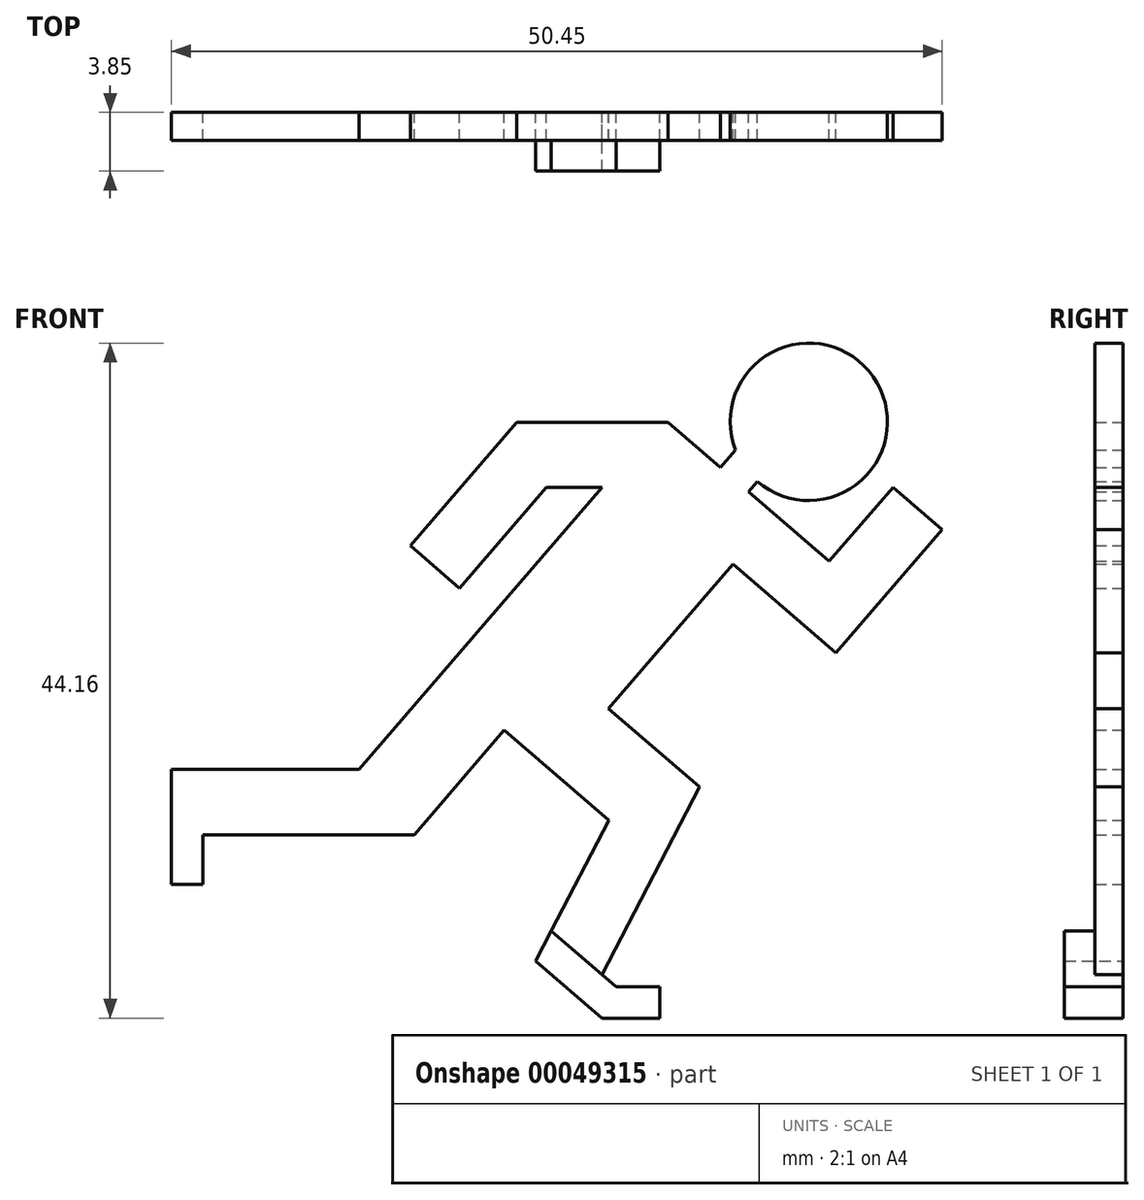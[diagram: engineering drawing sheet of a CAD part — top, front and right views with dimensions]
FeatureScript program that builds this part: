
annotation { "Feature Type Name" : "Feature", "Feature Type Description" : "" }
export const myFeature = defineFeature(function(context is Context, id is Id, definition is map)
    precondition{}
    {
        {
            var Q0;
            Q0=qCreatedBy(makeId("Front.planeOp"),FACE);
            var sketch = newSketch(context, id + "F0", { "sketchPlane" : qUnion([Q0])});
            skCircle(sketch, "E0", {"center": v(13.54, 39.01) * mm, "radius": 5.15 * mm});
            skLineSegment(sketch, "E1", {"start": v(0, 0) * mm, "end": v(3.79, 0) * mm});
            skLineSegment(sketch, "E2", {"start": v(3.79, 0) * mm, "end": v(3.79, 2.06) * mm});
            skLineSegment(sketch, "E3", {"start": v(3.79, 2.06) * mm, "end": v(0.92, 2.06) * mm});
            skLineSegment(sketch, "E4", {"start": v(0.92, 2.06) * mm, "end": v(0, 2.85) * mm});
            skLineSegment(sketch, "E5", {"start": v(0, 2.85) * mm, "end": v(6.38, 15.12) * mm});
            skLineSegment(sketch, "E6", {"start": v(6.38, 15.12) * mm, "end": v(0.43, 20.24) * mm});
            skLineSegment(sketch, "E7", {"start": v(0.43, 20.24) * mm, "end": v(8.57, 29.7) * mm});
            skLineSegment(sketch, "E8", {"start": v(8.57, 29.7) * mm, "end": v(15.32, 23.88) * mm});
            skLineSegment(sketch, "E9", {"start": v(15.32, 23.88) * mm, "end": v(22.27, 31.95) * mm});
            skLineSegment(sketch, "E10", {"start": v(22.27, 31.95) * mm, "end": v(19.04, 34.73) * mm});
            skLineSegment(sketch, "E11", {"start": v(19.04, 34.73) * mm, "end": v(14.87, 29.89) * mm});
            skLineSegment(sketch, "E12", {"start": v(14.87, 29.89) * mm, "end": v(4.32, 38.97) * mm});
            skLineSegment(sketch, "E13", {"start": v(4.32, 38.97) * mm, "end": v(-5.59, 38.97) * mm});
            skLineSegment(sketch, "E14", {"start": v(-5.59, 38.97) * mm, "end": v(-12.54, 30.9) * mm});
            skLineSegment(sketch, "E15", {"start": v(-12.54, 30.9) * mm, "end": v(-9.31, 28.12) * mm});
            skLineSegment(sketch, "E16", {"start": v(-9.31, 28.12) * mm, "end": v(-3.64, 34.71) * mm});
            skLineSegment(sketch, "E17", {"start": v(-3.64, 34.71) * mm, "end": v(0, 34.71) * mm});
            skLineSegment(sketch, "E18", {"start": v(0, 34.71) * mm, "end": v(-15.9, 16.26) * mm});
            skLineSegment(sketch, "E19", {"start": v(-15.9, 16.26) * mm, "end": v(-28.18, 16.26) * mm});
            skLineSegment(sketch, "E20", {"start": v(-28.18, 16.26) * mm, "end": v(-28.18, 8.74) * mm});
            skLineSegment(sketch, "E21", {"start": v(-28.18, 8.74) * mm, "end": v(-26.12, 8.74) * mm});
            skLineSegment(sketch, "E22", {"start": v(-26.12, 8.74) * mm, "end": v(-26.12, 12) * mm});
            skLineSegment(sketch, "E23", {"start": v(-26.12, 12) * mm, "end": v(-12.29, 12) * mm});
            skLineSegment(sketch, "E24", {"start": v(-12.29, 12) * mm, "end": v(-6.4, 18.85) * mm});
            skLineSegment(sketch, "E25", {"start": v(-6.4, 18.85) * mm, "end": v(0.45, 12.95) * mm});
            skLineSegment(sketch, "E26", {"start": v(0.45, 12.95) * mm, "end": v(-4.34, 3.74) * mm});
            skLineSegment(sketch, "E27", {"start": v(-4.34, 3.74) * mm, "end": v(0, 0) * mm});
            skLineSegment(sketch, "E28", {"start": v(0, 34.71) * mm, "end": v(0, 38.97) * mm, "construction": true});
            skLineSegment(sketch, "E29", {"start": v(14.87, 29.89) * mm, "end": v(12.1, 26.66) * mm, "construction": true});
            skLineSegment(sketch, "E30", {"start": v(0.45, 12.95) * mm, "end": v(4.05, 17.13) * mm, "construction": true});
            skLineSegment(sketch, "E31", {"start": v(0.45, 12.95) * mm, "end": v(4.23, 10.99) * mm, "construction": true});
            skLineSegment(sketch, "E32", {"start": v(-15.9, 16.26) * mm, "end": v(-15.9, 12) * mm, "construction": true});
            skLineSegment(sketch, "E33", {"start": v(-6.4, 18.85) * mm, "end": v(-10.57, 22.44) * mm, "construction": true});
            skLineSegment(sketch, "E34", {"start": v(7.74, 36.03) * mm, "end": v(8.73, 37.18) * mm});
            skLineSegment(sketch, "E35", {"start": v(9.6, 34.43) * mm, "end": v(10.18, 35.1) * mm});
            skSolve(sketch);
        }
        {
            var Q0;
            Q0 = qSketchRegion(id + "F0", true);
            extrude(context, id + "F1", {"entities" : qUnion([Q0]), "depth" : 1.85 * mm});
        }
        {
            var Q0;
            Q0=makeQuery(id+"F1.opExtrude","CAP_FACE",FACE,{"disambiguationData":[OSD([sQuery(id+"F0.wireOp",EDGE,"E0"),sQuery(id+"F0.wireOp",EDGE,"E1"),sQuery(id+"F0.wireOp",EDGE,"E2"),sQuery(id+"F0.wireOp",EDGE,"E3"),sQuery(id+"F0.wireOp",EDGE,"E4"),sQuery(id+"F0.wireOp",EDGE,"E5"),sQuery(id+"F0.wireOp",EDGE,"E6"),sQuery(id+"F0.wireOp",EDGE,"E7"),sQuery(id+"F0.wireOp",EDGE,"E8"),sQuery(id+"F0.wireOp",EDGE,"E9"),sQuery(id+"F0.wireOp",EDGE,"E10"),sQuery(id+"F0.wireOp",EDGE,"E11"),sQuery(id+"F0.wireOp",EDGE,"E12"),sQuery(id+"F0.wireOp",EDGE,"E13"),sQuery(id+"F0.wireOp",EDGE,"E14"),sQuery(id+"F0.wireOp",EDGE,"E15"),sQuery(id+"F0.wireOp",EDGE,"E16"),sQuery(id+"F0.wireOp",EDGE,"E17"),sQuery(id+"F0.wireOp",EDGE,"E18"),sQuery(id+"F0.wireOp",EDGE,"E19"),sQuery(id+"F0.wireOp",EDGE,"E20"),sQuery(id+"F0.wireOp",EDGE,"E21"),sQuery(id+"F0.wireOp",EDGE,"E22"),sQuery(id+"F0.wireOp",EDGE,"E23"),sQuery(id+"F0.wireOp",EDGE,"E24"),sQuery(id+"F0.wireOp",EDGE,"E25"),sQuery(id+"F0.wireOp",EDGE,"E26"),sQuery(id+"F0.wireOp",EDGE,"E27"),sQuery(id+"F0.wireOp",EDGE,"E34"),sQuery(id+"F0.wireOp",EDGE,"E35")])],"isStart":false});
            var sketch = newSketch(context, id + "F2", { "sketchPlane" : qUnion([Q0])});
            skLineSegment(sketch, "E36", {"start": v(0, 0) * mm, "end": v(3.79, 0) * mm});
            skLineSegment(sketch, "E37", {"start": v(3.79, 0) * mm, "end": v(3.79, 2.06) * mm});
            skLineSegment(sketch, "E38", {"start": v(3.79, 2.06) * mm, "end": v(0.92, 2.06) * mm});
            skLineSegment(sketch, "E39", {"start": v(0.92, 2.06) * mm, "end": v(-3.32, 5.7) * mm});
            skLineSegment(sketch, "E40", {"start": v(-3.32, 5.7) * mm, "end": v(-4.34, 3.74) * mm});
            skLineSegment(sketch, "E41", {"start": v(-4.34, 3.74) * mm, "end": v(0, 0) * mm});
            skSolve(sketch);
        }
        {
            var Q0;
            Q0 = qSketchRegion(id + "F2", true);
            extrude(context, id + "F3", {"entities" : qUnion([Q0]), "operationType" : NewBodyOperationType.ADD, "depth" : 2 * mm});
        }
    });
